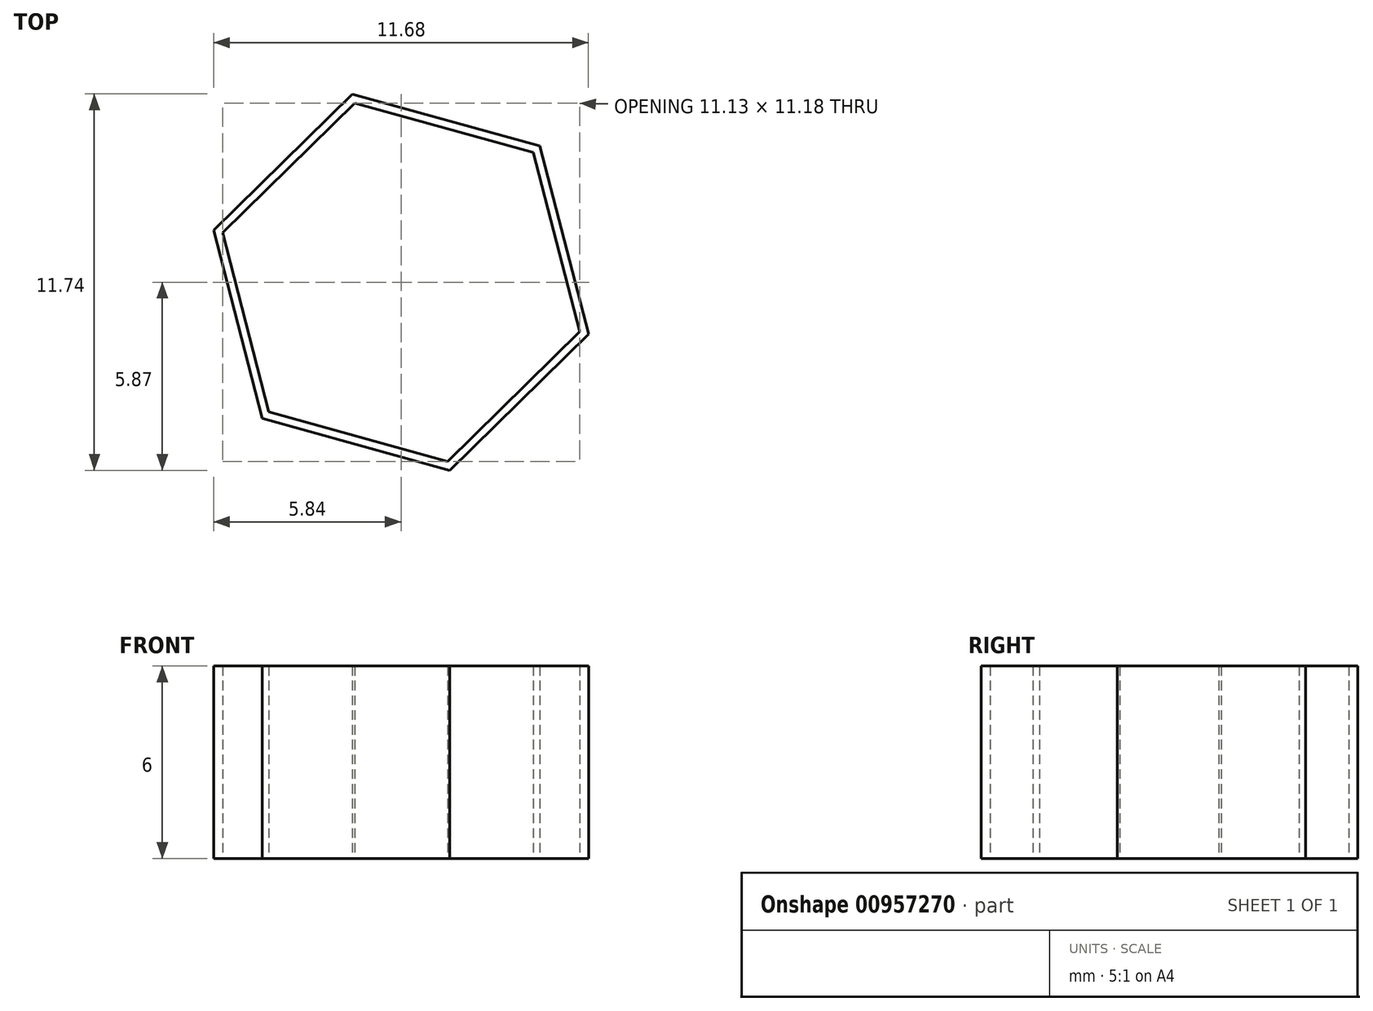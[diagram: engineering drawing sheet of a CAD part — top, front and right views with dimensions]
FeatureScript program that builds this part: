
annotation { "Feature Type Name" : "Feature", "Feature Type Description" : "" }
export const myFeature = defineFeature(function(context is Context, id is Id, definition is map)
    precondition{}
    {
        {
            var Q0;
            Q0=qCreatedBy(makeId("Top.planeOp"),FACE);
            var sketch = newSketch(context, id + "F0", { "sketchPlane" : qUnion([Q0])});
            skCircle(sketch, "E0.cCircle", {"center": v(0, 0) * mm, "radius": 5 * mm, "construction": true});
            skLineSegment(sketch, "E0.0", {"start": v(5.56, -1.54) * mm, "end": v(1.45, -5.59) * mm});
            skLineSegment(sketch, "E0.1", {"start": v(1.45, -5.59) * mm, "end": v(-4.12, -4.05) * mm});
            skLineSegment(sketch, "E0.2", {"start": v(-4.12, -4.05) * mm, "end": v(-5.56, 1.54) * mm});
            skLineSegment(sketch, "E0.3", {"start": v(-5.56, 1.54) * mm, "end": v(-1.45, 5.59) * mm});
            skLineSegment(sketch, "E0.4", {"start": v(-1.45, 5.59) * mm, "end": v(4.12, 4.05) * mm});
            skLineSegment(sketch, "E0.5", {"start": v(4.12, 4.05) * mm, "end": v(5.56, -1.54) * mm});
            skPoint(sketch, "E0.0.midPoint", {"position": v(3.5, -3.57) * mm});
            skCircle(sketch, "E1.cCircle", {"center": v(0, 0) * mm, "radius": 5.25 * mm, "construction": true});
            skLineSegment(sketch, "E1.0", {"start": v(5.84, -1.62) * mm, "end": v(1.52, -5.87) * mm});
            skLineSegment(sketch, "E1.1", {"start": v(1.52, -5.87) * mm, "end": v(-4.32, -4.25) * mm});
            skLineSegment(sketch, "E1.2", {"start": v(-4.32, -4.25) * mm, "end": v(-5.84, 1.62) * mm});
            skLineSegment(sketch, "E1.3", {"start": v(-5.84, 1.62) * mm, "end": v(-1.52, 5.87) * mm});
            skLineSegment(sketch, "E1.4", {"start": v(-1.52, 5.87) * mm, "end": v(4.32, 4.25) * mm});
            skLineSegment(sketch, "E1.5", {"start": v(4.32, 4.25) * mm, "end": v(5.84, -1.62) * mm});
            skPoint(sketch, "E1.0.midPoint", {"position": v(3.68, -3.74) * mm});
            skSolve(sketch);
        }
        {
            var Q0;
            Q0=makeQuery(id+"F0.imprint","IMPRINT",FACE,{"disambiguationData":[TD([[makeQuery(id+"F0.imprint","IMPRINT",EDGE,{"derivedFrom":sQuery(id+"F0.wireOp",EDGE,"E0.0")}),1.0]])]});
            extrude(context, id + "F1", {"entities" : qUnion([Q0]), "depth" : 6 * mm, "offsetDistance" : 25 * mm});
        }
    });
